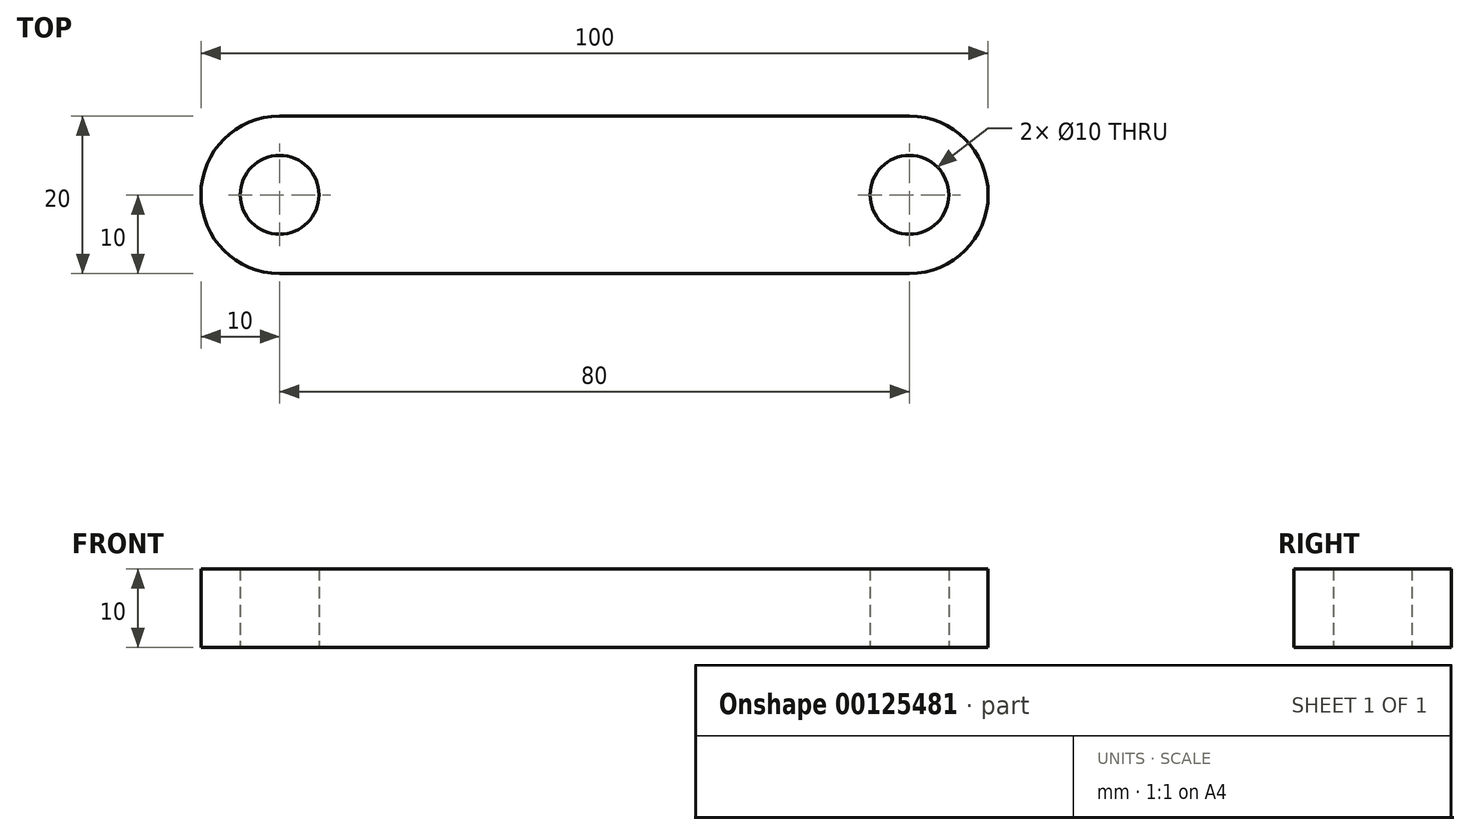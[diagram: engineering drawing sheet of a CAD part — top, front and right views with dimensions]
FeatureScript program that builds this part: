
annotation { "Feature Type Name" : "Feature", "Feature Type Description" : "" }
export const myFeature = defineFeature(function(context is Context, id is Id, definition is map)
    precondition{}
    {
        {
            var Q0;
            Q0=qCreatedBy(makeId("Top.planeOp"),FACE);
            var sketch = newSketch(context, id + "F0", { "sketchPlane" : qUnion([Q0])});
            skLineSegment(sketch, "E0", {"start": v(0, 0) * mm, "end": v(80, 0) * mm});
            skLineSegment(sketch, "E1", {"start": v(0, 20) * mm, "end": v(80, 20) * mm});
            skArc(sketch, "E2", {"start": v(0, 20) * mm, "mid": v(-10, 10) * mm, "end": v(0, 0) * mm});
            skArc(sketch, "E3", {"start": v(80, 0) * mm, "mid": v(90, 10) * mm, "end": v(80, 20) * mm});
            skSolve(sketch);
        }
        {
            var Q0;
            Q0 = qSketchRegion(id + "F0", true);
            extrude(context, id + "F1", {"entities" : qUnion([Q0]), "depth" : 10 * mm});
        }
        {
            var Q0;
            Q0=qCreatedBy(makeId("Top.planeOp"),FACE);
            var sketch = newSketch(context, id + "F2", { "sketchPlane" : qUnion([Q0])});
            skCircle(sketch, "E4", {"center": v(0, 10) * mm, "radius": 5 * mm});
            skCircle(sketch, "E5.1.0.0", {"center": v(80, 10) * mm, "radius": 5 * mm});
            skLineSegment(sketch, "E5.direction1", {"start": v(0, 10) * mm, "end": v(80, 10) * mm, "construction": true});
            skSolve(sketch);
        }
        {
            var Q0;
            Q0 = qSketchRegion(id + "F2", true);
            extrude(context, id + "F3", {"entities" : qUnion([Q0]), "operationType" : NewBodyOperationType.REMOVE, "depth" : 25 * mm});
        }
    });
